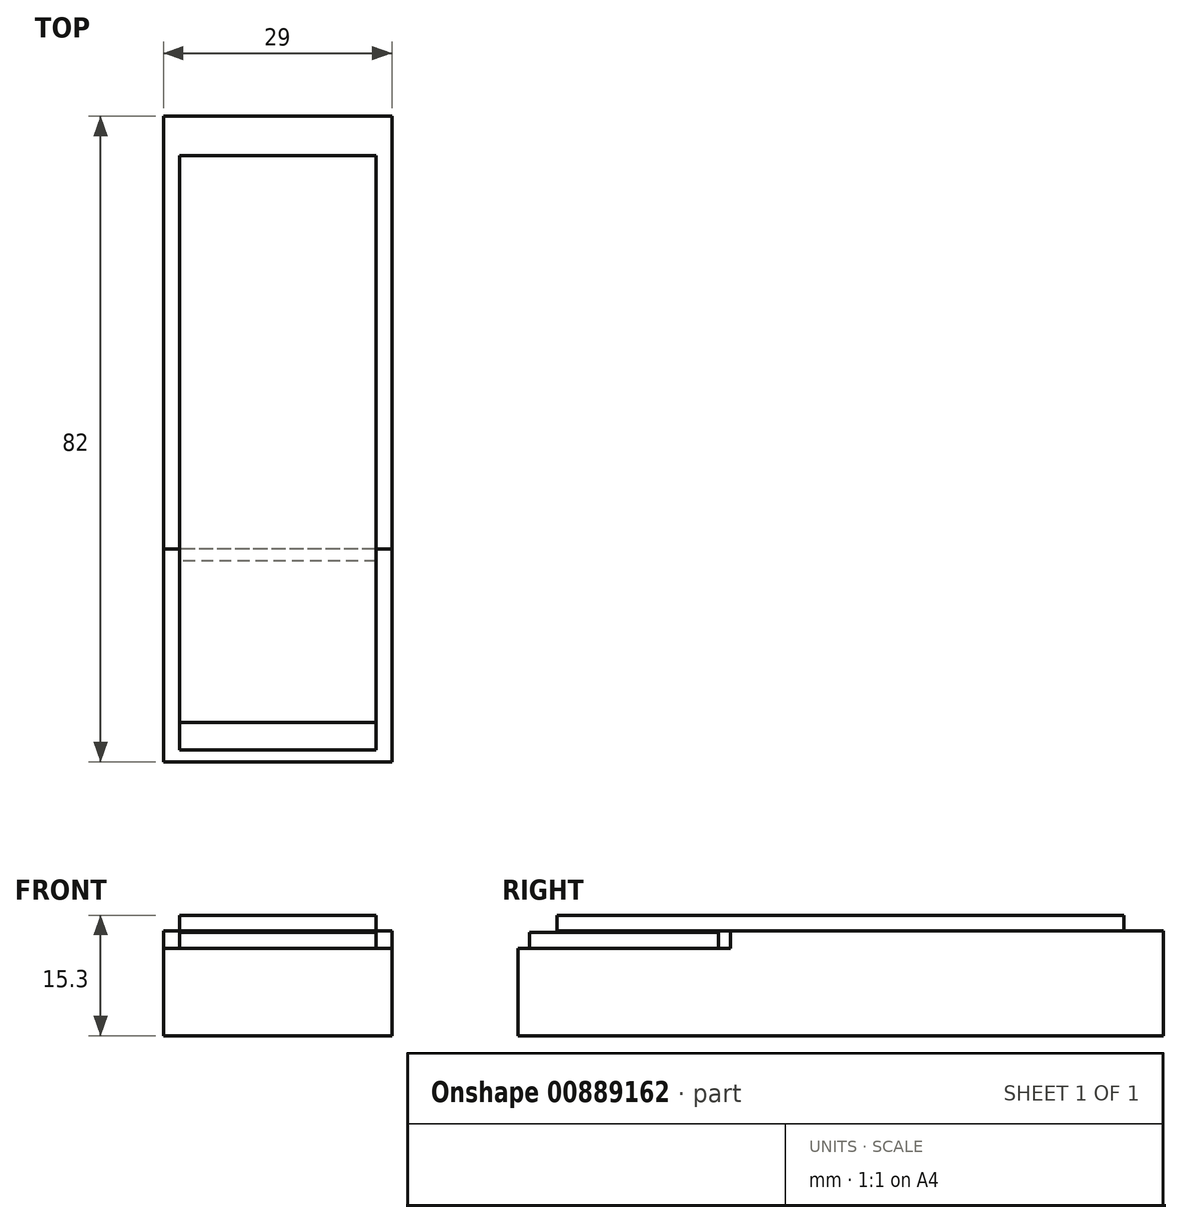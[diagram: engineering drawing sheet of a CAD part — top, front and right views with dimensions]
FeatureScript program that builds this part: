
annotation { "Feature Type Name" : "Feature", "Feature Type Description" : "" }
export const myFeature = defineFeature(function(context is Context, id is Id, definition is map)
    precondition{}
    {
        {
            assignVariable(context, id + "F0", {"name" : "body_w", "anyValue" : 29});
        }
        {
            var Q0;
            Q0=qCreatedBy(makeId("Right.planeOp"),FACE);
            var sketch = newSketch(context, id + "F1", { "sketchPlane" : qUnion([Q0])});
            skLineSegment(sketch, "E0.bottom", {"start": v(27, 7.75) * mm, "end": v(82, 7.75) * mm});
            skLineSegment(sketch, "E0.top", {"start": v(0, -5.55) * mm, "end": v(82, -5.55) * mm});
            skLineSegment(sketch, "E0.left", {"start": v(0, 5.55) * mm, "end": v(0, -5.55) * mm});
            skLineSegment(sketch, "E0.right", {"start": v(82, 7.75) * mm, "end": v(82, -5.55) * mm});
            skLineSegment(sketch, "E1", {"start": v(27, 7.75) * mm, "end": v(27, 5.55) * mm});
            skLineSegment(sketch, "E2", {"start": v(27, 5.55) * mm, "end": v(0, 5.55) * mm});
            skPoint(sketch, "E3", {"position": v(41, 7.75) * mm});
            skPoint(sketch, "E4", {"position": v(41, -5.55) * mm});
            skPoint(sketch, "E5", {"position": v(0, 7.75) * mm});
            skSolve(sketch);
        }
        {
            var Q0;
            Q0=qCreatedBy(makeId("Right.planeOp"),FACE);
            var sketch = newSketch(context, id + "F2", { "sketchPlane" : qUnion([Q0])});
            skLineSegment(sketch, "E6.bottom", {"start": v(1.5, 7.55) * mm, "end": v(25.5, 7.55) * mm});
            skLineSegment(sketch, "E6.top", {"start": v(1.5, 5.55) * mm, "end": v(25.5, 5.55) * mm});
            skLineSegment(sketch, "E6.left", {"start": v(1.5, 7.55) * mm, "end": v(1.5, 5.55) * mm});
            skLineSegment(sketch, "E6.right", {"start": v(25.5, 7.55) * mm, "end": v(25.5, 5.55) * mm});
            skLineSegment(sketch, "E7.bottom", {"start": v(5, 9.75) * mm, "end": v(77, 9.75) * mm});
            skLineSegment(sketch, "E7.top", {"start": v(5, 7.75) * mm, "end": v(77, 7.75) * mm});
            skLineSegment(sketch, "E7.left", {"start": v(5, 9.75) * mm, "end": v(5, 7.75) * mm});
            skLineSegment(sketch, "E7.right", {"start": v(77, 9.75) * mm, "end": v(77, 7.75) * mm});
            skPoint(sketch, "E8", {"position": v(41, 9.75) * mm});
            skPoint(sketch, "E9", {"position": v(0, 9.75) * mm});
            skSolve(sketch);
        }
        {
            var Q0;
            Q0=makeQuery(id+"F1.imprint","IMPRINT",FACE,{"disambiguationData":[TD([[makeQuery(id+"F1.imprint","IMPRINT",EDGE,{"derivedFrom":sQuery(id+"F1.wireOp",EDGE,"E0.bottom")}),-1.0]])]});
            extrude(context, id + "F3", {"entities" : qUnion([Q0]), "endBound" : BoundingType.SYMMETRIC, "depth" : (getVariable(context, 'body_w')) * mm, "offsetDistance" : 25 * mm});
        }
        {
            var Q0;
            Q0=makeQuery(id+"F2.imprint","IMPRINT",FACE,{"disambiguationData":[TD([[makeQuery(id+"F2.imprint","IMPRINT",EDGE,{"derivedFrom":sQuery(id+"F2.wireOp",EDGE,"E6.bottom")}),-1.0]])]});
            extrude(context, id + "F4", {"entities" : qUnion([Q0]), "endBound" : BoundingType.SYMMETRIC, "depth" : (getVariable(context, 'body_w') - 4) * mm, "offsetDistance" : 25 * mm});
        }
        {
            var Q0;
            Q0=makeQuery(id+"F2.imprint","IMPRINT",FACE,{"disambiguationData":[TD([[makeQuery(id+"F2.imprint","IMPRINT",EDGE,{"derivedFrom":sQuery(id+"F2.wireOp",EDGE,"E7.bottom")}),-1.0]])]});
            extrude(context, id + "F5", {"entities" : qUnion([Q0]), "endBound" : BoundingType.SYMMETRIC, "depth" : (getVariable(context, 'body_w') - 4) * mm, "offsetDistance" : 25 * mm});
        }
    });
